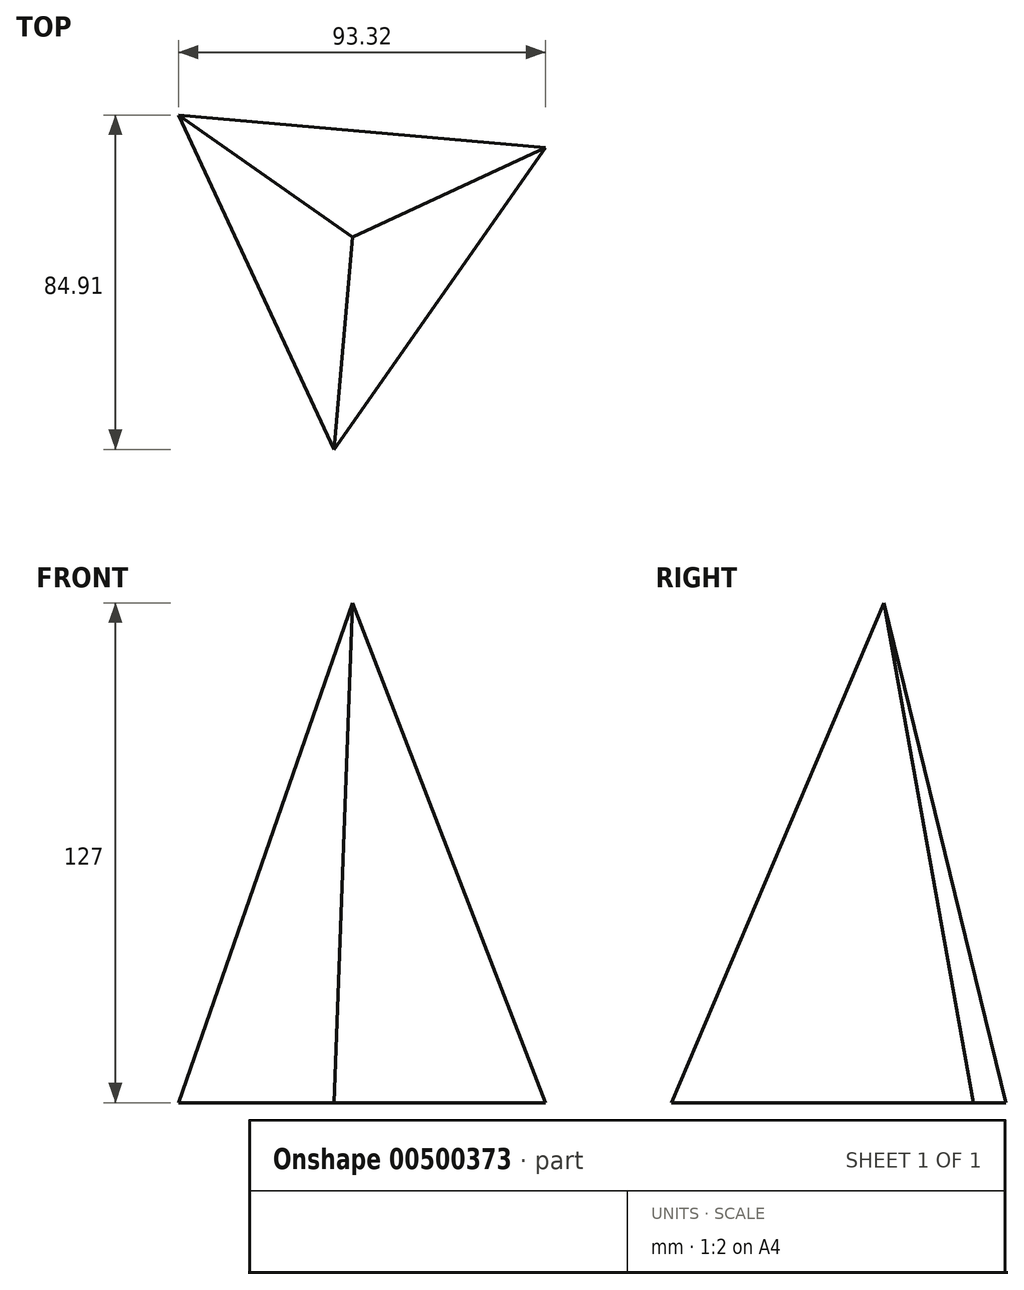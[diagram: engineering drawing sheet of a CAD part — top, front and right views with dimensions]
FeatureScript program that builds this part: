
annotation { "Feature Type Name" : "Feature", "Feature Type Description" : "" }
export const myFeature = defineFeature(function(context is Context, id is Id, definition is map)
    precondition{}
    {
        {
            var Q0;
            Q0=qCreatedBy(makeId("Top.planeOp"),FACE);
            var sketch = newSketch(context, id + "F0", { "sketchPlane" : qUnion([Q0])});
            skCircle(sketch, "E0.cCircle", {"center": v(0, 0) * mm, "radius": 54.08 * mm, "construction": true});
            skLineSegment(sketch, "E0.0", {"start": v(-44.29, 31.04) * mm, "end": v(49.03, 22.83) * mm});
            skLineSegment(sketch, "E0.1", {"start": v(49.03, 22.83) * mm, "end": v(-4.74, -53.87) * mm});
            skLineSegment(sketch, "E0.2", {"start": v(-4.74, -53.87) * mm, "end": v(-44.29, 31.04) * mm});
            skSolve(sketch);
        }
        {
            var Q0;
            Q0=qCreatedBy(makeId("Top.planeOp"),FACE);
            cPlane(context, id + "F1", {"entities" : qUnion([Q0]), "cplaneType" : CPlaneType.OFFSET, "offset" : 127 * mm, "width" : 152.4 * mm, "height" : 152.4 * mm});
        }
        {
            var Q0;
            Q0=qCreatedBy(id+"F1.planeOp",FACE);
            var sketch = newSketch(context, id + "F2", { "sketchPlane" : qUnion([Q0])});
            skPoint(sketch, "E1", {"position": v(0, 0) * mm});
            skSolve(sketch);
        }
        {
            var Q0;
            Q0=makeQuery(id+"F0.imprint","IMPRINT",FACE,{"disambiguationData":[TD([[makeQuery(id+"F0.imprint","IMPRINT",EDGE,{"derivedFrom":sQuery(id+"F0.wireOp",EDGE,"E0.0")}),-1.0]])]});
            var Q1;
            Q1=sQuery(id+"F2.wireOp",VERTEX,"E1");
            loft(context, id + "F3", {"sheetProfilesArray" : [{ "sheetProfileEntities" : qUnion([Q0]) }, { "sheetProfileEntities" : qUnion([Q1]) }]});
        }
    });
